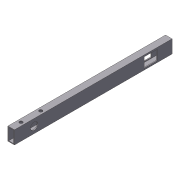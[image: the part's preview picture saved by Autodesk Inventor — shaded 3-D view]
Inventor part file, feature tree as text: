
AUTODESK INVENTOR PART (.ipt)
format: ipt  version: 2012 (Build 160160000, 160)  size: 123,392 bytes
history: native  units: in
note: dims shown in document units (in); Inventor stores cm internally (conversion verified against a paired STEP export)
features: extrude x4, sketch x4
ambient origin geometry x8: Origin, YZ Plane, XZ Plane, XY Plane, X Axis, Y Axis, Z Axis, Center Point
bodies: Solid1 (feature_tree)
feature tree (8):
  extrude  "Extrusion1"  Depth=2.0in
  extrude  "Extrusion2"  Depth=1.75in
  extrude  "Extrusion5"  Depth=0.125in
  extrude  "Extrusion6"  Depth=2.25in
  sketch  "Sketch1"  dims[d0=1.0in d1=2.0in]
  sketch  "Sketch2"  dims[d2=0.75in d3=1.75in]
  sketch  "Sketch5"  dims[d4=0.125in d5=0.125in]
  sketch  "Sketch6"  dims[d6=24.0in d7=0.0in d12=2.25in d21=4.25in d25=24.0in d26=0.0in d29=2.0in d32=1.5in d33=0.25in d53=1.5in d54=3.0in d55=0.5in d56=0.5in d57=0.25in d58=1.0in d59=0.0in d60=0.5in d61=0.5in d62=1.0in d63=0.0in d64=1.125in d65=3.0in d66=1.0in]
